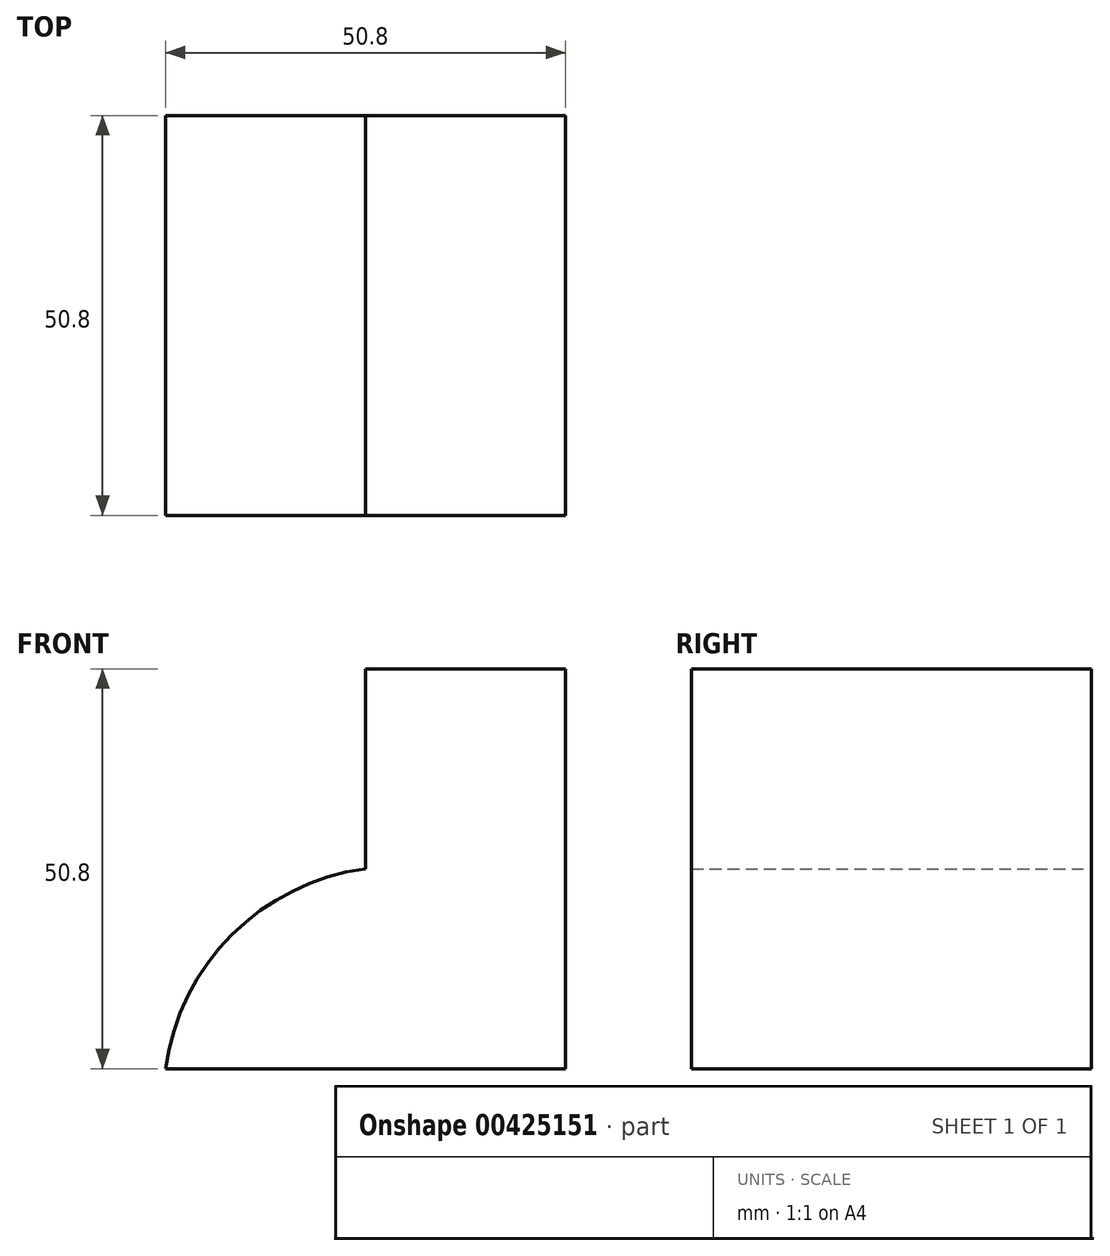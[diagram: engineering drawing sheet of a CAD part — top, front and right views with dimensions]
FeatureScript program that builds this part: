
annotation { "Feature Type Name" : "Feature", "Feature Type Description" : "" }
export const myFeature = defineFeature(function(context is Context, id is Id, definition is map)
    precondition{}
    {
        {
            var Q0;
            Q0=qCreatedBy(makeId("Front.planeOp"),FACE);
            var sketch = newSketch(context, id + "F0", { "sketchPlane" : qUnion([Q0])});
            skLineSegment(sketch, "E0", {"start": v(0, 0) * mm, "end": v(50.8, 0) * mm});
            skLineSegment(sketch, "E1", {"start": v(50.8, 0) * mm, "end": v(50.8, 50.8) * mm});
            skLineSegment(sketch, "E2", {"start": v(50.8, 50.8) * mm, "end": v(25.4, 50.8) * mm});
            skLineSegment(sketch, "E3", {"start": v(25.4, 50.8) * mm, "end": v(25.4, 25.4) * mm});
            skArc(sketch, "E4", {"start": v(25.4, 25.4) * mm, "mid": v(8.4, 17) * mm, "end": v(0, 0) * mm});
            skSolve(sketch);
        }
        {
            var Q0;
            Q0 = qSketchRegion(id + "F0", true);
            extrude(context, id + "F1", {"entities" : qUnion([Q0]), "depth" : 50.8 * mm});
        }
    });
